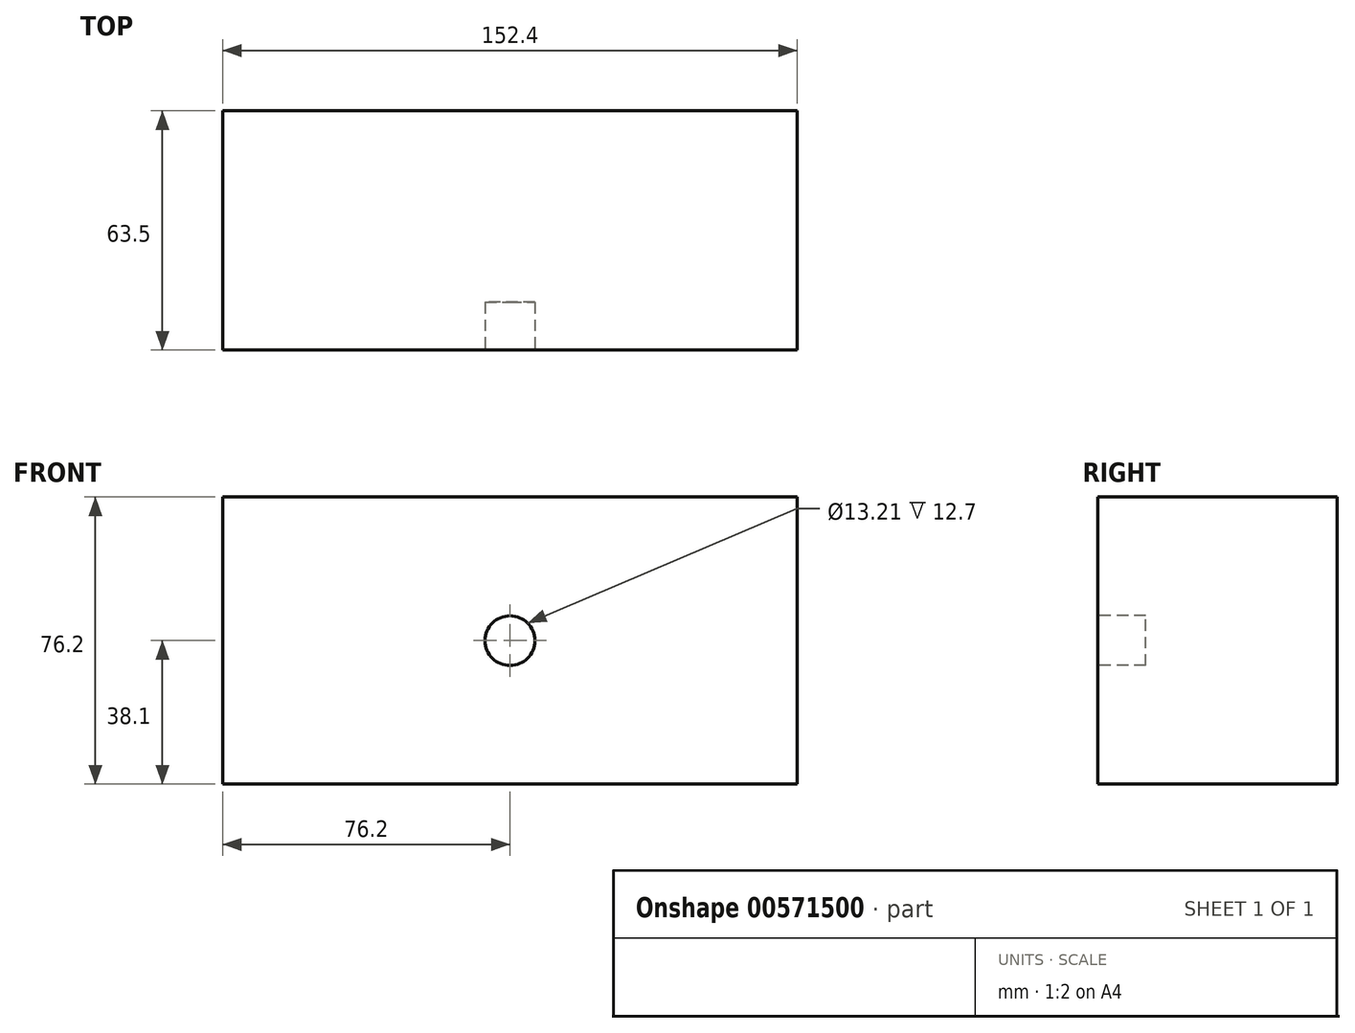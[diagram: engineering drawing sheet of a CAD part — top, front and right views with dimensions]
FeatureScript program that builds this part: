
annotation { "Feature Type Name" : "Feature", "Feature Type Description" : "" }
export const myFeature = defineFeature(function(context is Context, id is Id, definition is map)
    precondition{}
    {
        {
            var Q0;
            Q0=qCreatedBy(makeId("Top.planeOp"),FACE);
            var sketch = newSketch(context, id + "F0", { "sketchPlane" : qUnion([Q0])});
            skLineSegment(sketch, "E0.bottom", {"start": v(0, 0) * mm, "end": v(152.4, 0) * mm});
            skLineSegment(sketch, "E0.top", {"start": v(0, 63.5) * mm, "end": v(152.4, 63.5) * mm});
            skLineSegment(sketch, "E0.left", {"start": v(0, 0) * mm, "end": v(0, 63.5) * mm});
            skLineSegment(sketch, "E0.right", {"start": v(152.4, 0) * mm, "end": v(152.4, 63.5) * mm});
            skSolve(sketch);
        }
        {
            var Q0;
            Q0=makeQuery(id+"F0.imprint","IMPRINT",FACE,{"disambiguationData":[TD([[makeQuery(id+"F0.imprint","IMPRINT",EDGE,{"derivedFrom":sQuery(id+"F0.wireOp",EDGE,"E0.bottom")}),1.0]])]});
            var Q1;
            Q1 = qSketchRegion(id + "F2", true);
            extrude(context, id + "F1", {"entities" : qUnion([Q0, Q1]), "depth" : 76.2 * mm, "offsetDistance" : 25.4 * mm});
        }
        {
            var Q0;
            Q0=makeQuery(id+"F1.opExtrude","SWEPT_FACE",FACE,{"disambiguationData":[OSD([sQuery(id+"F0.wireOp",EDGE,"E0.bottom")])]});
            var sketch = newSketch(context, id + "F2", { "sketchPlane" : qUnion([Q0])});
            skCircle(sketch, "E1", {"center": v(76.2, 38.1) * mm, "radius": 6.6 * mm});
            skSolve(sketch);
        }
        {
            var Q0;
            Q0=makeQuery(id+"F2.imprint","IMPRINT",FACE,{"disambiguationData":[TD([[makeQuery(id+"F2.imprint","IMPRINT",EDGE,{"derivedFrom":sQuery(id+"F2.wireOp",EDGE,"E1")}),1.0]])]});
            extrude(context, id + "F3", {"entities" : qUnion([Q0]), "operationType" : NewBodyOperationType.REMOVE, "oppositeDirection" : true, "depth" : 12.7 * mm, "offsetDistance" : 25.4 * mm});
        }
    });
